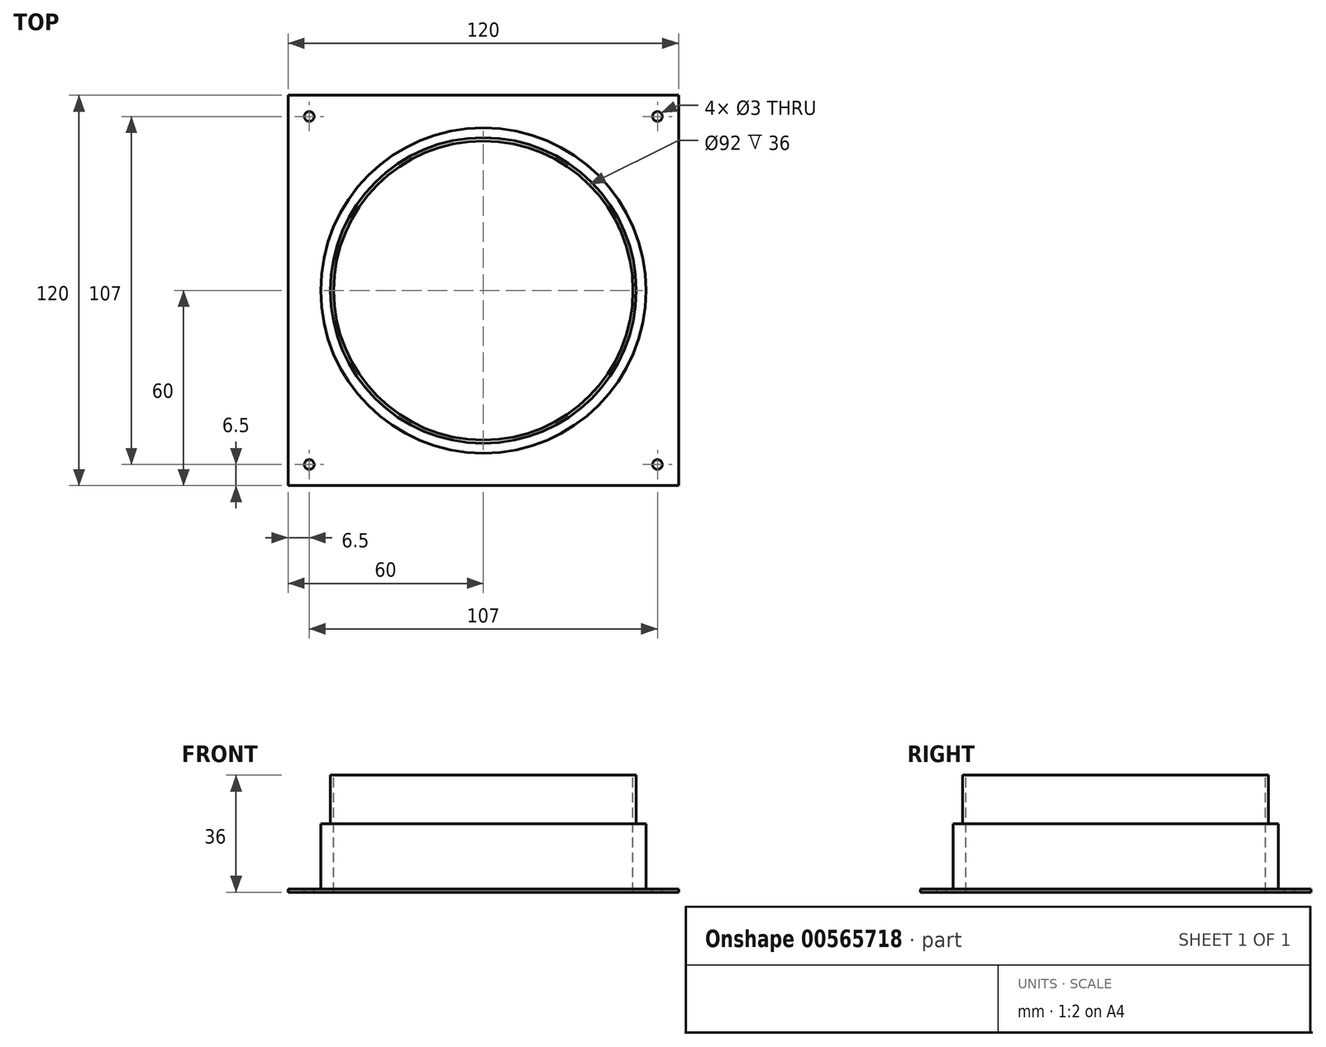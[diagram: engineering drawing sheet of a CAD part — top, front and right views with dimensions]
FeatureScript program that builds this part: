
annotation { "Feature Type Name" : "Feature", "Feature Type Description" : "" }
export const myFeature = defineFeature(function(context is Context, id is Id, definition is map)
    precondition{}
    {
        {
            var Q0;
            Q0=qCreatedBy(makeId("Top.planeOp"),FACE);
            var sketch = newSketch(context, id + "F0", { "sketchPlane" : qUnion([Q0])});
            skLineSegment(sketch, "E0.bottom", {"start": v(-60, 60) * mm, "end": v(60, 60) * mm});
            skLineSegment(sketch, "E0.top", {"start": v(-60, -60) * mm, "end": v(60, -60) * mm});
            skLineSegment(sketch, "E0.left", {"start": v(-60, 60) * mm, "end": v(-60, -60) * mm});
            skLineSegment(sketch, "E0.right", {"start": v(60, 60) * mm, "end": v(60, -60) * mm});
            skPoint(sketch, "E0.middle", {"position": v(0, 0) * mm});
            skSolve(sketch);
        }
        {
            var Q0;
            Q0=makeQuery(id+"F0.imprint","IMPRINT",FACE,{"disambiguationData":[TD([[makeQuery(id+"F0.imprint","IMPRINT",EDGE,{"derivedFrom":sQuery(id+"F0.wireOp",EDGE,"E0.bottom")}),-1.0]])]});
            extrude(context, id + "F1", {"entities" : qUnion([Q0]), "depth" : 1 * mm, "offsetDistance" : 25 * mm});
        }
        {
            var Q0;
            Q0=makeQuery(id+"F1.opExtrude","CAP_FACE",FACE,{"disambiguationData":[OSD([sQuery(id+"F0.wireOp",EDGE,"E0.bottom"),sQuery(id+"F0.wireOp",EDGE,"E0.top"),sQuery(id+"F0.wireOp",EDGE,"E0.left"),sQuery(id+"F0.wireOp",EDGE,"E0.right")])],"isStart":false});
            var sketch = newSketch(context, id + "F2", { "sketchPlane" : qUnion([Q0])});
            skCircle(sketch, "E1", {"center": v(0, 0) * mm, "radius": 50 * mm});
            skSolve(sketch);
        }
        {
            var Q0;
            Q0=makeQuery(id+"F2.imprint","IMPRINT",FACE,{"disambiguationData":[TD([[makeQuery(id+"F2.imprint","IMPRINT",EDGE,{"derivedFrom":sQuery(id+"F2.wireOp",EDGE,"E1")}),1.0]])]});
            extrude(context, id + "F3", {"entities" : qUnion([Q0]), "operationType" : NewBodyOperationType.ADD, "depth" : 20 * mm, "offsetDistance" : 25 * mm});
        }
        {
            var Q0;
            Q0=makeQuery(id+"F3.opExtrude","CAP_FACE",FACE,{"disambiguationData":[OSD([sQuery(id+"F2.wireOp",EDGE,"E1")])],"isStart":false});
            var sketch = newSketch(context, id + "F4", { "sketchPlane" : qUnion([Q0])});
            skCircle(sketch, "E2", {"center": v(0, 0) * mm, "radius": 47 * mm});
            skSolve(sketch);
        }
        {
            var Q0;
            Q0=makeQuery(id+"F4.imprint","IMPRINT",FACE,{"disambiguationData":[TD([[makeQuery(id+"F4.imprint","IMPRINT",EDGE,{"derivedFrom":sQuery(id+"F4.wireOp",EDGE,"E2")}),1.0]])]});
            extrude(context, id + "F5", {"entities" : qUnion([Q0]), "operationType" : NewBodyOperationType.ADD, "depth" : 15 * mm, "offsetDistance" : 25 * mm});
        }
        {
            var Q0;
            Q0=makeQuery(id+"F5.opExtrude","CAP_FACE",FACE,{"disambiguationData":[OSD([sQuery(id+"F4.wireOp",EDGE,"E2")])],"isStart":false});
            var sketch = newSketch(context, id + "F6", { "sketchPlane" : qUnion([Q0])});
            skCircle(sketch, "E3", {"center": v(0, 0) * mm, "radius": 46 * mm});
            skSolve(sketch);
        }
        {
            var Q0;
            Q0=makeQuery(id+"F6.imprint","IMPRINT",FACE,{"disambiguationData":[TD([[makeQuery(id+"F6.imprint","IMPRINT",EDGE,{"derivedFrom":sQuery(id+"F6.wireOp",EDGE,"E3")}),1.0]])]});
            extrude(context, id + "F7", {"entities" : qUnion([Q0]), "operationType" : NewBodyOperationType.REMOVE, "oppositeDirection" : true, "depth" : 56.8 * mm, "offsetDistance" : 25 * mm});
        }
        {
            var Q0;
            Q0=makeQuery(id+"F1.opExtrude","CAP_FACE",FACE,{"disambiguationData":[OSD([sQuery(id+"F0.wireOp",EDGE,"E0.bottom"),sQuery(id+"F0.wireOp",EDGE,"E0.top"),sQuery(id+"F0.wireOp",EDGE,"E0.left"),sQuery(id+"F0.wireOp",EDGE,"E0.right")])],"isStart":false});
            var sketch = newSketch(context, id + "F8", { "sketchPlane" : qUnion([Q0])});
            skCircle(sketch, "E4", {"center": v(-53.5, 53.5) * mm, "radius": 1.5 * mm});
            skCircle(sketch, "E5.1.0", {"center": v(-53.5, -53.5) * mm, "radius": 1.5 * mm});
            skCircle(sketch, "E5.2.0", {"center": v(53.5, -53.5) * mm, "radius": 1.5 * mm});
            skCircle(sketch, "E5.3.0", {"center": v(53.5, 53.5) * mm, "radius": 1.5 * mm});
            skPoint(sketch, "E5.center", {"position": v(0, 0) * mm});
            skSolve(sketch);
        }
        {
            var Q0;
            Q0=makeQuery(id+"F8.imprint","IMPRINT",FACE,{"disambiguationData":[TD([[makeQuery(id+"F8.imprint","IMPRINT",EDGE,{"derivedFrom":sQuery(id+"F8.wireOp",EDGE,"E5.1.0")}),1.0]])]});
            var Q1;
            Q1=makeQuery(id+"F8.imprint","IMPRINT",FACE,{"disambiguationData":[TD([[makeQuery(id+"F8.imprint","IMPRINT",EDGE,{"derivedFrom":sQuery(id+"F8.wireOp",EDGE,"E5.2.0")}),1.0]])]});
            var Q2;
            Q2=makeQuery(id+"F8.imprint","IMPRINT",FACE,{"disambiguationData":[TD([[makeQuery(id+"F8.imprint","IMPRINT",EDGE,{"derivedFrom":sQuery(id+"F8.wireOp",EDGE,"E4")}),1.0]])]});
            var Q3;
            Q3=makeQuery(id+"F8.imprint","IMPRINT",FACE,{"disambiguationData":[TD([[makeQuery(id+"F8.imprint","IMPRINT",EDGE,{"derivedFrom":sQuery(id+"F8.wireOp",EDGE,"E5.3.0")}),1.0]])]});
            extrude(context, id + "F9", {"entities" : qUnion([Q0, Q1, Q2, Q3]), "operationType" : NewBodyOperationType.REMOVE, "oppositeDirection" : true, "depth" : 25 * mm, "offsetDistance" : 25 * mm});
        }
    });
